FCSTD DOCUMENT  (FreeCAD 1.0R39109 (Git))
Label: customfoil
License: All rights reserved
LicenseURL: https://en.wikipedia.org/wiki/All_rights_reserved
objects: Sketcher::SketchObject×1, PartDesign::Body×1
note: 3 computed .brp shape members not serialized (recipe doc carries the construction recipe); baked Part::Feature solids carry a one-line shape summary decoded from their .brp

FEATURE [Sketcher::SketchObject] Sketch
  ArcFitTolerance = 1e-06
  AttachmentSupport = -> [XZ_Plane]
  FullyConstrained = true
  MakeInternals = false
  MapMode = 5
  Placement = pos=(0,0,0) rot=(1,0,0;1.5708rad)
  sketch-geometry (16):
    g0-g3: Circle [constr] x4 (B-spline internal-alignment scaffolding for g4; pole/knot coordinates omitted)
    g4: BSplineCurve PolesCount=4 KnotsCount=2 Degree=3 IsPeriodic=0
    g5: GeomPoint [constr] X=0 Y=0 Z=0
    g6: GeomPoint [constr] X=1000 Y=-21 Z=0
    g7-g10: Circle [constr] x4 (B-spline internal-alignment scaffolding for g11; pole/knot coordinates omitted)
    g11: BSplineCurve PolesCount=4 KnotsCount=2 Degree=3 IsPeriodic=0
    g12: GeomPoint [constr] X=0 Y=0 Z=0
    g13: GeomPoint [constr] X=1000 Y=-21 Z=0
    g14: GeomPoint X=-500 Y=0 Z=0
    g15: GeomPoint X=0 Y=-500 Z=0
  constraints (31):
    c: Weight(g0) = 1
    c: Equal(g0,g1)
    c: Equal(g0,g2)
    c: Equal(g0,g3)
    c: InternalAlignment(g0-g3 -> g4) x4
    c: InternalAlignment(g5,g4)
    c: InternalAlignment(g6,g4)
    c: Coincident(g0,g-1)
    c: Weight(g7) = 1
    c: Equal(g7,g8)
    c: Equal(g7,g9)
    c: Equal(g7,g10)
    c: InternalAlignment(g7-g10 -> g11) x4
    c: InternalAlignment(g12,g11)
    c: InternalAlignment(g13,g11)
    c: Coincident(g7,g4)
    c: Coincident(g10,g4)
    c: Horizontal(g14,g11)
    c: DistanceX(g14,g-1) = 500
    c: DistanceX(g11,g11) = 1000
    c: PointOnObject(g15,g-2)
    c: DistanceY(g15,g-1) = 500
    c: DistanceY(g15,g8) = 32  'y1L'
    c: DistanceY(g15,g9) = 260  'y2L'
    c: DistanceX(g14,g1) = 735  'x1U'
    c: DistanceX(g14,g2) = 1246  'x2U'
    c: DistanceX(g14,g8) = 547  'x1L'
    c: DistanceX(g14,g9) = 1254  'x2L'
    c: DistanceY(g11,g1) = 234  'y1U'
    c: DistanceY(g11,g2) = 214  'y2U'
    c: DistanceY(g15,g11) = 479  'yTE'
FEATURE [PartDesign::Body] Body
  AllowCompound = false
  Group = -> [Sketch]
  Origin = -> Origin
